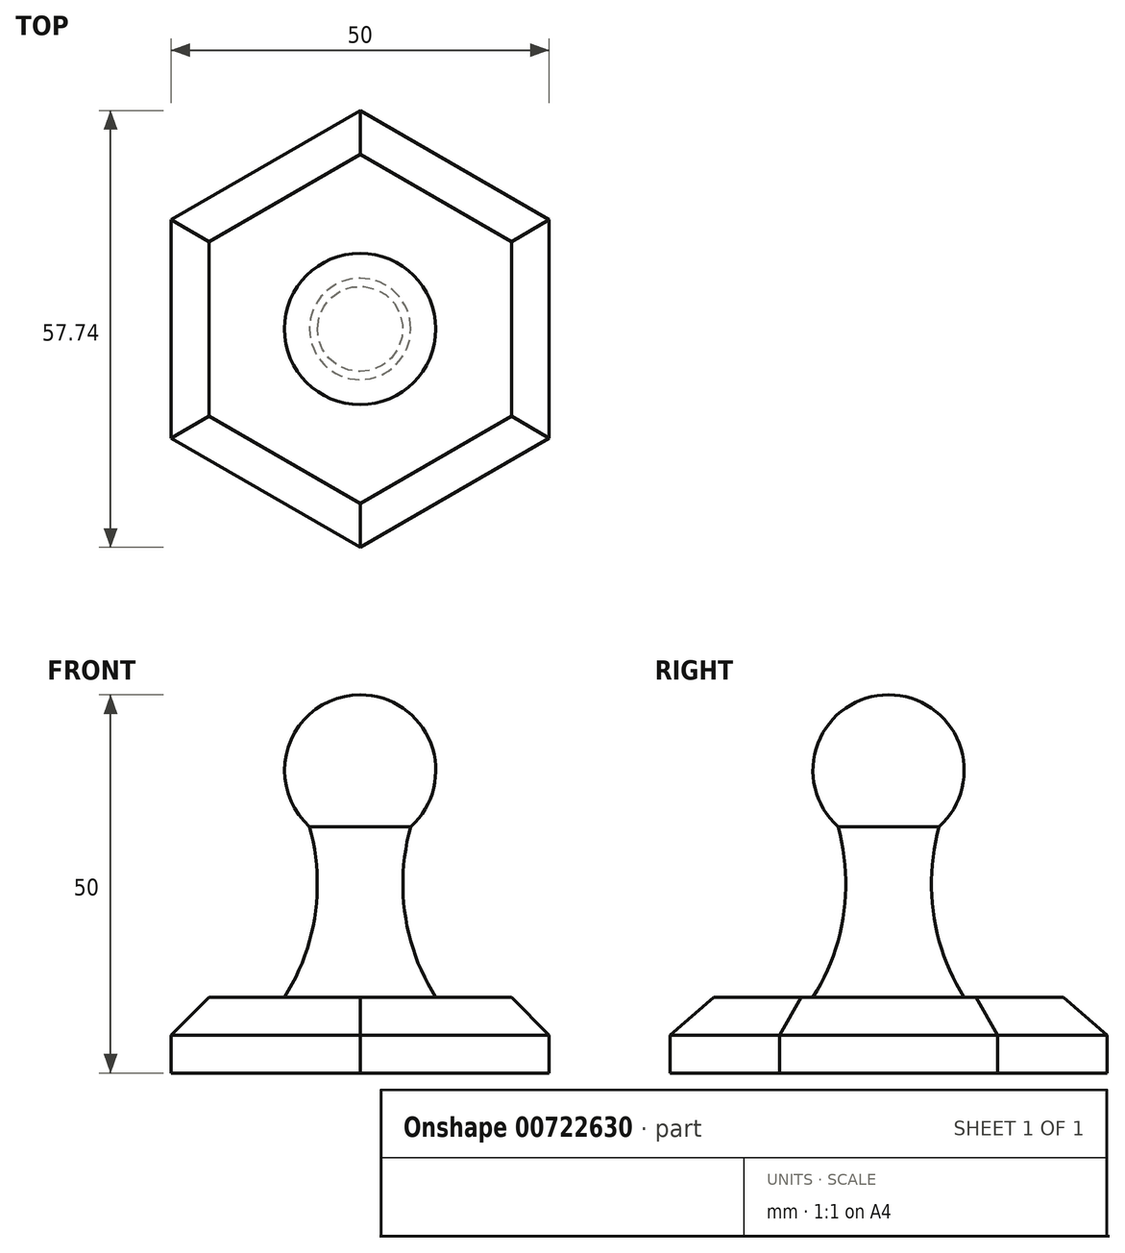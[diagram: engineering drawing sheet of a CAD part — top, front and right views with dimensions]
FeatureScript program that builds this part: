
annotation { "Feature Type Name" : "Feature", "Feature Type Description" : "" }
export const myFeature = defineFeature(function(context is Context, id is Id, definition is map)
    precondition{}
    {
        {
            var Q0;
            Q0=qCreatedBy(makeId("Top.planeOp"),FACE);
            var sketch = newSketch(context, id + "F0", { "sketchPlane" : qUnion([Q0])});
            skCircle(sketch, "E0.cCircle", {"center": v(0, 0) * mm, "radius": 25 * mm, "construction": true});
            skLineSegment(sketch, "E0.0", {"start": v(-25, -14.43) * mm, "end": v(-25, 14.43) * mm});
            skLineSegment(sketch, "E0.1", {"start": v(-25, 14.43) * mm, "end": v(0, 28.87) * mm});
            skLineSegment(sketch, "E0.2", {"start": v(0, 28.87) * mm, "end": v(25, 14.43) * mm});
            skLineSegment(sketch, "E0.3", {"start": v(25, 14.43) * mm, "end": v(25, -14.43) * mm});
            skLineSegment(sketch, "E0.4", {"start": v(25, -14.43) * mm, "end": v(0, -28.87) * mm});
            skLineSegment(sketch, "E0.5", {"start": v(0, -28.87) * mm, "end": v(-25, -14.43) * mm});
            skPoint(sketch, "E0.0.midPoint", {"position": v(-25, 0) * mm});
            skSolve(sketch);
        }
        {
            var Q0;
            Q0=makeQuery(id+"F0.imprint","IMPRINT",FACE,{"disambiguationData":[TD([[makeQuery(id+"F0.imprint","IMPRINT",EDGE,{"derivedFrom":sQuery(id+"F0.wireOp",EDGE,"E0.0")}),-1.0]])]});
            extrude(context, id + "F1", {"entities" : qUnion([Q0]), "depth" : 10 * mm, "offsetDistance" : 25 * mm});
        }
        {
            var Q0;
            Q0=qCreatedBy(makeId("Front.planeOp"),FACE);
            var sketch = newSketch(context, id + "F2", { "sketchPlane" : qUnion([Q0])});
            skCircle(sketch, "E1", {"center": v(0, 40) * mm, "radius": 10 * mm});
            skLineSegment(sketch, "E2.0", {"start": v(25, 10) * mm, "end": v(0, 10) * mm});
            skLineSegment(sketch, "E3.0", {"start": v(0, 10) * mm, "end": v(-25, 10) * mm});
            skLineSegment(sketch, "E4", {"start": v(-10, 40) * mm, "end": v(-10, 10) * mm, "construction": true});
            skLineSegment(sketch, "E5", {"start": v(10, 40) * mm, "end": v(10, 10) * mm, "construction": true});
            skArc(sketch, "E6", {"start": v(-10, 10) * mm, "mid": v(-5.65, 25) * mm, "end": v(-10, 40) * mm});
            skLineSegment(sketch, "E7", {"start": v(0, 10) * mm, "end": v(0, 50) * mm});
            skSolve(sketch);
        }
        {
            var Q0;
            {var subQ0=sQuery(id+"F2.wireOp",EDGE,"E6");var subQ1=sQuery(id+"F2.wireOp",EDGE,"E1");var subQ2=makeQuery(id+"F2.imprint","INTERSECT",VERTEX,{"disambiguationData":[OD(1.0)],"derivedFrom":[subQ1,subQ0]});Q0=makeQuery(id+"F2.imprint","IMPRINT",FACE,{"disambiguationData":[TD([[makeQuery(id+"F2.imprint","IMPRINT",EDGE,{"disambiguationData":[TD([[subQ2,-1.0]])],"derivedFrom":subQ1}),-1.0]])]});}
            var Q1;
            {var subQ0=sQuery(id+"F2.wireOp",EDGE,"E6");var subQ1=sQuery(id+"F2.wireOp",EDGE,"E1");var subQ2=makeQuery(id+"F2.imprint","INTERSECT",VERTEX,{"disambiguationData":[OD(0.0)],"derivedFrom":[subQ1,subQ0]});Q1=makeQuery(id+"F2.imprint","IMPRINT",FACE,{"disambiguationData":[TD([[makeQuery(id+"F2.imprint","IMPRINT",EDGE,{"disambiguationData":[TD([[subQ2,1.0]])],"derivedFrom":subQ1}),1.0]])]});}
            var Q2;
            {var subQ0=sQuery(id+"F2.wireOp",EDGE,"E6");var subQ1=sQuery(id+"F2.wireOp",EDGE,"E1");var subQ2=makeQuery(id+"F2.imprint","INTERSECT",VERTEX,{"disambiguationData":[OD(0.0)],"derivedFrom":[subQ1,subQ0]});Q2=makeQuery(id+"F2.imprint","IMPRINT",FACE,{"disambiguationData":[TD([[makeQuery(id+"F2.imprint","IMPRINT",EDGE,{"disambiguationData":[TD([[subQ2,-1.0]])],"derivedFrom":subQ1}),1.0]])]});}
            var Q3;
            Q3=sQuery(id+"F2.wireOp",EDGE,"E7");
            revolve(context, id + "F3", {"operationType" : NewBodyOperationType.ADD, "surfaceOperationType" : NewSurfaceOperationType.NEW, "entities" : qUnion([Q0, Q1, Q2]), "axis" : qUnion([Q3]), "revolveType" : RevolveType.FULL});
        }
        {
            var Q0;
            Q0=makeQuery(id+"F1.opExtrude","CAP_EDGE",EDGE,{"disambiguationData":[OSD([sQuery(id+"F0.wireOp",EDGE,"E0.0")])],"isStart":false});
            var Q1;
            Q1=makeQuery(id+"F1.opExtrude","CAP_EDGE",EDGE,{"disambiguationData":[OSD([sQuery(id+"F0.wireOp",EDGE,"E0.5")])],"isStart":false});
            var Q2;
            Q2=makeQuery(id+"F1.opExtrude","CAP_EDGE",EDGE,{"disambiguationData":[OSD([sQuery(id+"F0.wireOp",EDGE,"E0.1")])],"isStart":false});
            var Q3;
            Q3=makeQuery(id+"F1.opExtrude","CAP_EDGE",EDGE,{"disambiguationData":[OSD([sQuery(id+"F0.wireOp",EDGE,"E0.2")])],"isStart":false});
            var Q4;
            Q4=makeQuery(id+"F1.opExtrude","CAP_EDGE",EDGE,{"disambiguationData":[OSD([sQuery(id+"F0.wireOp",EDGE,"E0.3")])],"isStart":false});
            var Q5;
            Q5=makeQuery(id+"F1.opExtrude","CAP_EDGE",EDGE,{"disambiguationData":[OSD([sQuery(id+"F0.wireOp",EDGE,"E0.4")])],"isStart":false});
            chamfer(context, id + "F4", {"entities" : qUnion([Q0, Q1, Q2, Q3, Q4, Q5]), "width" : 5 * mm, "tangentPropagation" : true});
        }
    });
